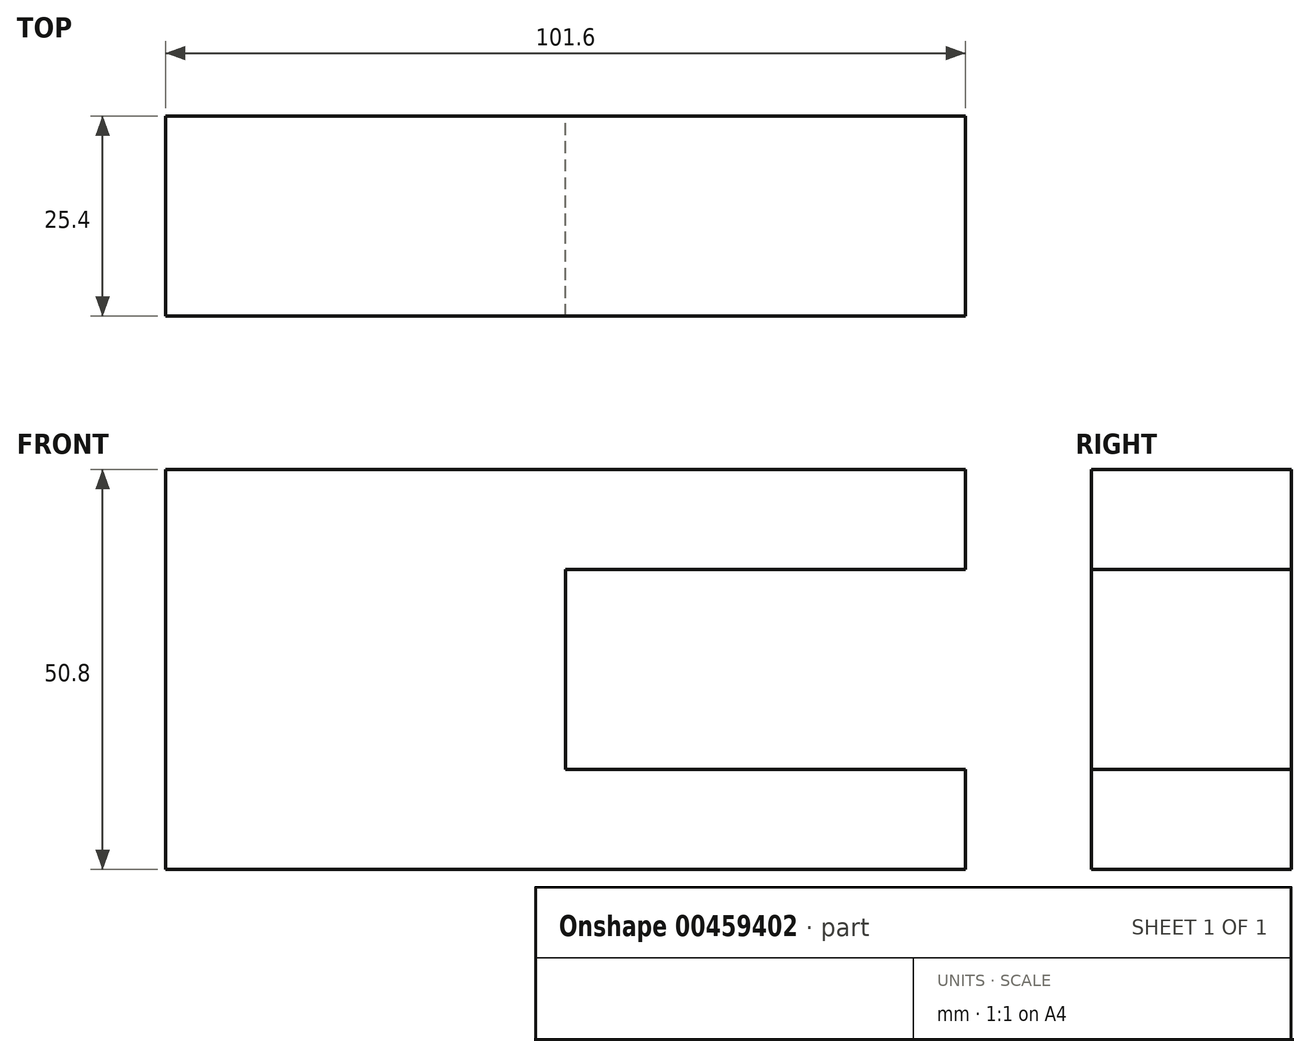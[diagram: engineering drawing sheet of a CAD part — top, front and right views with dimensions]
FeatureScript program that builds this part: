
annotation { "Feature Type Name" : "Feature", "Feature Type Description" : "" }
export const myFeature = defineFeature(function(context is Context, id is Id, definition is map)
    precondition{}
    {
        {
            var Q0;
            Q0=qCreatedBy(makeId("Front.planeOp"),FACE);
            var sketch = newSketch(context, id + "F0", { "sketchPlane" : qUnion([Q0])});
            skLineSegment(sketch, "E0.bottom", {"start": v(-50.8, 25.4) * mm, "end": v(50.8, 25.4) * mm});
            skLineSegment(sketch, "E0.top", {"start": v(-50.8, -25.4) * mm, "end": v(50.8, -25.4) * mm});
            skLineSegment(sketch, "E0.left", {"start": v(-50.8, 25.4) * mm, "end": v(-50.8, -25.4) * mm});
            skLineSegment(sketch, "E0.right", {"start": v(50.8, 25.4) * mm, "end": v(50.8, -25.4) * mm});
            skPoint(sketch, "E0.middle", {"position": v(0, 0) * mm});
            skSolve(sketch);
        }
        {
            var Q0;
            Q0 = qSketchRegion(id + "F0", true);
            extrude(context, id + "F1", {"entities" : qUnion([Q0]), "depth" : 25.4 * mm});
        }
        {
            var Q0;
            Q0=qCreatedBy(makeId("Front.planeOp"),FACE);
            var sketch = newSketch(context, id + "F2", { "sketchPlane" : qUnion([Q0])});
            skLineSegment(sketch, "E1.bottom", {"start": v(50.8, -12.7) * mm, "end": v(0, -12.7) * mm});
            skLineSegment(sketch, "E1.top", {"start": v(50.8, 12.7) * mm, "end": v(0, 12.7) * mm});
            skLineSegment(sketch, "E1.left", {"start": v(50.8, -12.7) * mm, "end": v(50.8, 12.7) * mm});
            skLineSegment(sketch, "E1.right", {"start": v(0, -12.7) * mm, "end": v(0, 12.7) * mm});
            skSolve(sketch);
        }
        {
            var Q0;
            Q0 = qSketchRegion(id + "F2", true);
            extrude(context, id + "F3", {"entities" : qUnion([Q0]), "operationType" : NewBodyOperationType.REMOVE, "endBound" : BoundingType.THROUGH_ALL, "oppositeDirection" : true, "depth" : 25.4 * mm});
        }
        {
            var Q0;
            Q0=makeQuery(id+"F2.imprint","IMPRINT",FACE,{"disambiguationData":[TD([[makeQuery(id+"F2.imprint","IMPRINT",EDGE,{"derivedFrom":sQuery(id+"F2.wireOp",EDGE,"E1.bottom")}),-1.0]])]});
            extrude(context, id + "F4", {"entities" : qUnion([Q0]), "operationType" : NewBodyOperationType.REMOVE, "endBound" : BoundingType.THROUGH_ALL, "depth" : 25.4 * mm});
        }
    });
